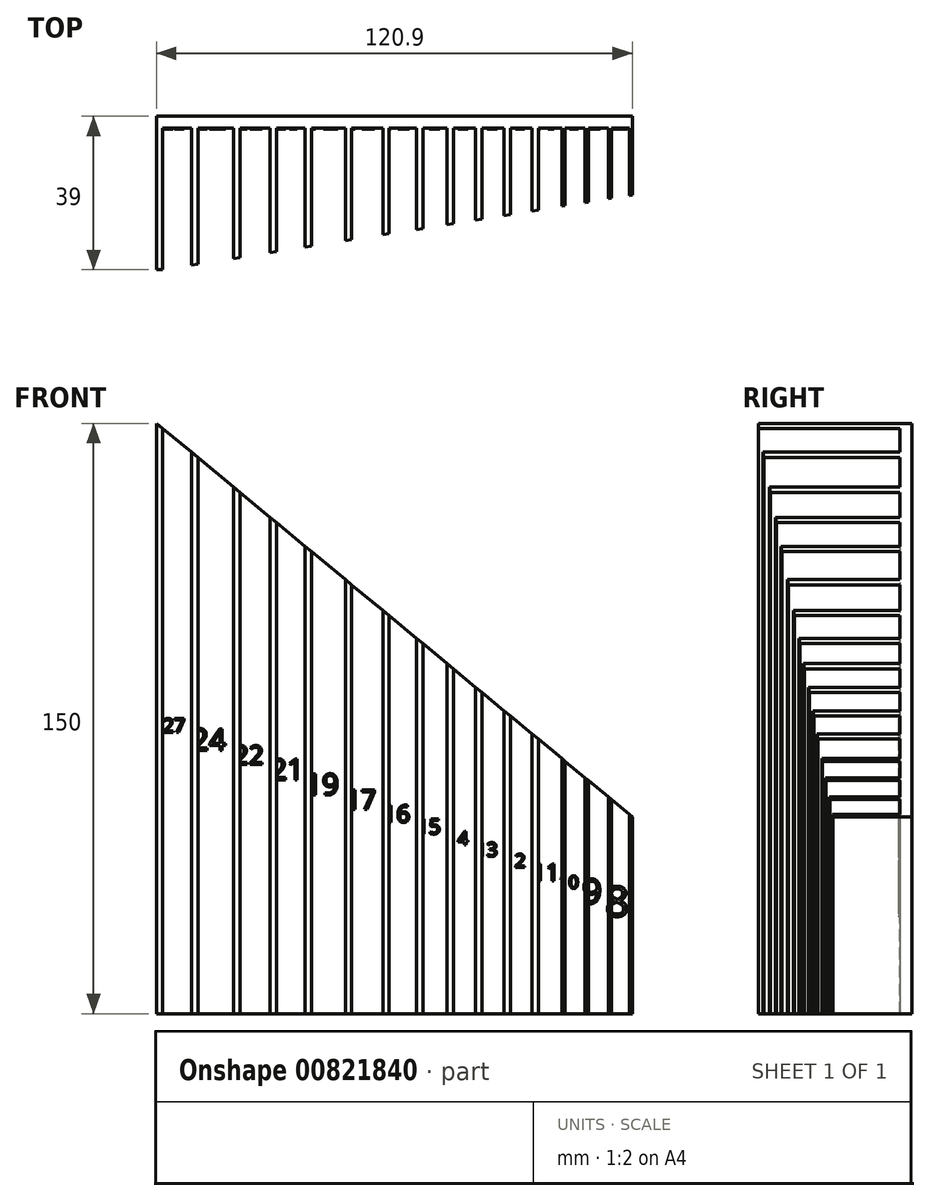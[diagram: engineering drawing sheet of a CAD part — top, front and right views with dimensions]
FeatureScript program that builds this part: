
annotation { "Feature Type Name" : "Feature", "Feature Type Description" : "" }
export const myFeature = defineFeature(function(context is Context, id is Id, definition is map)
    precondition{}
    {
        {
            var Q0;
            Q0=qCreatedBy(makeId("Front.planeOp"),FACE);
            var sketch = newSketch(context, id + "F0", { "sketchPlane" : qUnion([Q0])});
            skLineSegment(sketch, "E0", {"start": v(-64.3, 150) * mm, "end": v(-64.3, 0) * mm});
            skLineSegment(sketch, "E1", {"start": v(-64.3, 0) * mm, "end": v(56.6, 0) * mm});
            skLineSegment(sketch, "E2", {"start": v(56.6, 50) * mm, "end": v(-64.3, 150) * mm});
            skLineSegment(sketch, "E3", {"start": v(-64.3, 75) * mm, "end": v(56.6, 25) * mm, "construction": true});
            skLineSegment(sketch, "E4", {"start": v(56.6, 50) * mm, "end": v(56.6, 0) * mm});
            skSolve(sketch);
        }
        {
            var Q0;
            {var subQ0=sQuery(id+"F0.wireOp",EDGE,"E0");Q0=makeQuery(id+"F0.imprint","IMPRINT",FACE,{"disambiguationData":[TD([[makeQuery(id+"F0.imprint","IMPRINT",EDGE,{"derivedFrom":subQ0}),1.0]])]});}
            extrude(context, id + "F1", {"entities" : qUnion([Q0]), "depth" : 3 * mm, "offsetDistance" : 25 * mm});
        }
        {
            var Q0;
            Q0=makeQuery(id+"F1.opExtrude","CAP_FACE",FACE,{"disambiguationData":[OSD([sQuery(id+"F0.wireOp",EDGE,"E0"),sQuery(id+"F0.wireOp",EDGE,"E1"),sQuery(id+"F0.wireOp",EDGE,"0AxQtryP-TZW4-hSLZ-hSIb-DcVt68QFEk3i"),sQuery(id+"F0.wireOp",EDGE,"E2")])],"isStart":false});
            var sketch = newSketch(context, id + "F2", { "sketchPlane" : qUnion([Q0])});
            skLineSegment(sketch, "E5", {"start": v(-55.4, 142.64) * mm, "end": v(-55.4, 0) * mm});
            skLineSegment(sketch, "E6", {"start": v(-53.8, 141.32) * mm, "end": v(-53.8, 0) * mm});
            skLineSegment(sketch, "E7", {"start": v(-44.7, 133.79) * mm, "end": v(-44.7, 0) * mm});
            skLineSegment(sketch, "E8", {"start": v(-43.1, 132.46) * mm, "end": v(-43.1, 0) * mm});
            skLineSegment(sketch, "E9", {"start": v(-35.4, 126.1) * mm, "end": v(-35.4, 0) * mm});
            skLineSegment(sketch, "E10", {"start": v(-33.8, 124.77) * mm, "end": v(-33.8, 0) * mm});
            skLineSegment(sketch, "E11", {"start": v(-26.5, 118.73) * mm, "end": v(-26.5, 0) * mm});
            skLineSegment(sketch, "E12", {"start": v(-24.9, 117.41) * mm, "end": v(-24.9, 0) * mm});
            skLineSegment(sketch, "E13", {"start": v(-16.3, 110.3) * mm, "end": v(-16.3, 0) * mm});
            skLineSegment(sketch, "E14", {"start": v(-14.7, 108.97) * mm, "end": v(-14.7, 0) * mm});
            skLineSegment(sketch, "E15", {"start": v(-6.8, 102.44) * mm, "end": v(-6.8, 0) * mm});
            skLineSegment(sketch, "E16", {"start": v(-5.2, 101.12) * mm, "end": v(-5.2, 0) * mm});
            skLineSegment(sketch, "E17", {"start": v(1.8, 0) * mm, "end": v(1.8, 95.33) * mm});
            skLineSegment(sketch, "E18", {"start": v(3.4, 94) * mm, "end": v(3.4, 0) * mm});
            skLineSegment(sketch, "E19", {"start": v(9.5, 88.96) * mm, "end": v(9.5, 0) * mm});
            skLineSegment(sketch, "E20", {"start": v(11.1, 87.63) * mm, "end": v(11.1, 0) * mm});
            skLineSegment(sketch, "E21", {"start": v(16.8, 0) * mm, "end": v(16.8, 82.92) * mm});
            skLineSegment(sketch, "E22", {"start": v(18.4, 81.6) * mm, "end": v(18.4, 0) * mm});
            skLineSegment(sketch, "E23", {"start": v(24, 0) * mm, "end": v(24, 76.96) * mm});
            skLineSegment(sketch, "E24", {"start": v(25.6, 75.64) * mm, "end": v(25.6, 0) * mm});
            skLineSegment(sketch, "E25", {"start": v(31.1, 71.1) * mm, "end": v(31.1, 0) * mm});
            skLineSegment(sketch, "E26", {"start": v(32.7, 69.77) * mm, "end": v(32.7, 0) * mm});
            skLineSegment(sketch, "E27", {"start": v(38.7, 0) * mm, "end": v(38.7, 64.8) * mm});
            skLineSegment(sketch, "E28", {"start": v(39.5, 64.14) * mm, "end": v(39.5, 0) * mm});
            skLineSegment(sketch, "E29", {"start": v(44.6, 0) * mm, "end": v(44.6, 59.93) * mm});
            skLineSegment(sketch, "E30", {"start": v(45.4, 59.26) * mm, "end": v(45.4, 0) * mm});
            skLineSegment(sketch, "E31", {"start": v(50.5, 55.05) * mm, "end": v(50.5, 0) * mm});
            skLineSegment(sketch, "E32", {"start": v(51.3, 54.38) * mm, "end": v(51.3, 0) * mm});
            skLineSegment(sketch, "E33", {"start": v(-62.7, 148.68) * mm, "end": v(-62.7, 0) * mm});
            skLineSegment(sketch, "E34", {"start": v(55.8, 0) * mm, "end": v(55.8, 50.66) * mm});
            skSolve(sketch);
        }
        {
            var Q0;
            {var subQ0=sQuery(id+"F2.wireOp",EDGE,"E5");Q0=makeQuery(id+"F2.imprint","IMPRINT",FACE,{"disambiguationData":[TD([[makeQuery(id+"F2.imprint","IMPRINT",EDGE,{"derivedFrom":subQ0}),1.0]])]});}
            var Q1;
            {var subQ0=sQuery(id+"F2.wireOp",EDGE,"E7");Q1=makeQuery(id+"F2.imprint","IMPRINT",FACE,{"disambiguationData":[TD([[makeQuery(id+"F2.imprint","IMPRINT",EDGE,{"derivedFrom":subQ0}),1.0]])]});}
            var Q2;
            {var subQ0=sQuery(id+"F2.wireOp",EDGE,"E9");Q2=makeQuery(id+"F2.imprint","IMPRINT",FACE,{"disambiguationData":[TD([[makeQuery(id+"F2.imprint","IMPRINT",EDGE,{"derivedFrom":subQ0}),1.0]])]});}
            var Q3;
            {var subQ0=sQuery(id+"F2.wireOp",EDGE,"E11");Q3=makeQuery(id+"F2.imprint","IMPRINT",FACE,{"disambiguationData":[TD([[makeQuery(id+"F2.imprint","IMPRINT",EDGE,{"derivedFrom":subQ0}),1.0]])]});}
            var Q4;
            {var subQ0=sQuery(id+"F2.wireOp",EDGE,"E13");Q4=makeQuery(id+"F2.imprint","IMPRINT",FACE,{"disambiguationData":[TD([[makeQuery(id+"F2.imprint","IMPRINT",EDGE,{"derivedFrom":subQ0}),1.0]])]});}
            var Q5;
            {var subQ0=sQuery(id+"F2.wireOp",EDGE,"E15");Q5=makeQuery(id+"F2.imprint","IMPRINT",FACE,{"disambiguationData":[TD([[makeQuery(id+"F2.imprint","IMPRINT",EDGE,{"derivedFrom":subQ0}),1.0]])]});}
            var Q6;
            {var subQ0=sQuery(id+"F2.wireOp",EDGE,"E17");Q6=makeQuery(id+"F2.imprint","IMPRINT",FACE,{"disambiguationData":[TD([[makeQuery(id+"F2.imprint","IMPRINT",EDGE,{"derivedFrom":subQ0}),-1.0]])]});}
            var Q7;
            {var subQ0=sQuery(id+"F2.wireOp",EDGE,"E27");Q7=makeQuery(id+"F2.imprint","IMPRINT",FACE,{"disambiguationData":[TD([[makeQuery(id+"F2.imprint","IMPRINT",EDGE,{"derivedFrom":subQ0}),-1.0]])]});}
            var Q8;
            {var subQ0=sQuery(id+"F2.wireOp",EDGE,"E19");Q8=makeQuery(id+"F2.imprint","IMPRINT",FACE,{"disambiguationData":[TD([[makeQuery(id+"F2.imprint","IMPRINT",EDGE,{"derivedFrom":subQ0}),1.0]])]});}
            var Q9;
            {var subQ0=sQuery(id+"F2.wireOp",EDGE,"E21");Q9=makeQuery(id+"F2.imprint","IMPRINT",FACE,{"disambiguationData":[TD([[makeQuery(id+"F2.imprint","IMPRINT",EDGE,{"derivedFrom":subQ0}),-1.0]])]});}
            var Q10;
            {var subQ0=sQuery(id+"F2.wireOp",EDGE,"E23");Q10=makeQuery(id+"F2.imprint","IMPRINT",FACE,{"disambiguationData":[TD([[makeQuery(id+"F2.imprint","IMPRINT",EDGE,{"derivedFrom":subQ0}),-1.0]])]});}
            var Q11;
            {var subQ0=sQuery(id+"F2.wireOp",EDGE,"E25");Q11=makeQuery(id+"F2.imprint","IMPRINT",FACE,{"disambiguationData":[TD([[makeQuery(id+"F2.imprint","IMPRINT",EDGE,{"derivedFrom":subQ0}),1.0]])]});}
            var Q12;
            {var subQ0=sQuery(id+"F2.wireOp",EDGE,"E29");Q12=makeQuery(id+"F2.imprint","IMPRINT",FACE,{"disambiguationData":[TD([[makeQuery(id+"F2.imprint","IMPRINT",EDGE,{"derivedFrom":subQ0}),-1.0]])]});}
            var Q13;
            {var subQ0=sQuery(id+"F2.wireOp",EDGE,"E31");Q13=makeQuery(id+"F2.imprint","IMPRINT",FACE,{"disambiguationData":[TD([[makeQuery(id+"F2.imprint","IMPRINT",EDGE,{"derivedFrom":subQ0}),1.0]])]});}
            var Q14;
            {var subQ0=sQuery(id+"F2.wireOp",EDGE,"E34");Q14=makeQuery(id+"F2.imprint","IMPRINT",FACE,{"disambiguationData":[TD([[makeQuery(id+"F2.imprint","IMPRINT",EDGE,{"derivedFrom":subQ0}),-1.0]])]});}
            var Q15;
            {var subQ0=sQuery(id+"F2.wireOp",EDGE,"E33");Q15=makeQuery(id+"F2.imprint","IMPRINT",FACE,{"disambiguationData":[TD([[makeQuery(id+"F2.imprint","IMPRINT",EDGE,{"derivedFrom":subQ0}),-1.0]])]});}
            extrude(context, id + "F3", {"entities" : qUnion([Q0, Q1, Q2, Q3, Q4, Q5, Q6, Q7, Q8, Q9, Q10, Q11, Q12, Q13, Q14, Q15]), "operationType" : NewBodyOperationType.ADD, "depth" : 36 * mm, "offsetDistance" : 25 * mm});
        }
        {
            var Q0;
            Q0=qCreatedBy(makeId("Top.planeOp"),FACE);
            var sketch = newSketch(context, id + "F4", { "sketchPlane" : qUnion([Q0])});
            skLineSegment(sketch, "E35", {"start": v(-62.7, -39) * mm, "end": v(56.6, -20) * mm});
            skLineSegment(sketch, "E36", {"start": v(56.6, -39) * mm, "end": v(56.6, -20) * mm});
            skLineSegment(sketch, "E37", {"start": v(56.6, -39) * mm, "end": v(-62.7, -39) * mm});
            skSolve(sketch);
        }
        {
            var Q0;
            Q0 = qSketchRegion(id + "F4", true);
            extrude(context, id + "F5", {"entities" : qUnion([Q0]), "operationType" : NewBodyOperationType.REMOVE, "endBound" : BoundingType.THROUGH_ALL, "oppositeDirection" : true, "depth" : 25 * mm, "offsetDistance" : 25 * mm, "hasSecondDirection" : true, "secondDirectionBound" : SecondDirectionBoundingType.THROUGH_ALL, "secondDirectionOppositeDirection" : false, "secondDirectionDepth" : 25 * mm});
        }
        {
            var Q0;
            {var subQ0=sQuery(id+"F0.wireOp",EDGE,"E4");var subQ2=sQuery(id+"F0.wireOp",EDGE,"E2");var subQ5=sQuery(id+"F0.wireOp",EDGE,"E0");var subQ9=sQuery(id+"F0.wireOp",EDGE,"E1");var subQ34=sQuery(id+"F2.wireOp",EDGE,"E5");Q0=makeQuery(id+"F3.boolean.opBoolean","SPLIT",FACE,{"disambiguationData":[TD([makeQuery(id+"F3.opExtrude","SWEPT_FACE",FACE,{"disambiguationData":[OSD([subQ34])]})])],"derivedFrom":makeQuery(id+"F1.opExtrude","CAP_FACE",FACE,{"disambiguationData":[OSD([subQ5,subQ9,subQ2,subQ0])],"isStart":false})});}
            var sketch = newSketch(context, id + "F6", { "sketchPlane" : qUnion([Q0])});
            skLineSegment(sketch, "E38", {"start": v(-64.3, 75) * mm, "end": v(50.5, 27.52) * mm, "construction": true});
            skText(sketch, "E39", { "text": "27", "fontName": "OpenSans-Regular.ttf"});
            skText(sketch, "E40", { "text": "24\n", "fontName": "OpenSans-Regular.ttf"});
            skPoint(sketch, "E41", {"position": v(-49.25, 68.78) * mm});
            skPoint(sketch, "E42", {"position": v(-59.05, 72.83) * mm});
            skPoint(sketch, "E43", {"position": v(-39.25, 64.64) * mm});
            skPoint(sketch, "E44", {"position": v(-30.15, 60.88) * mm});
            skPoint(sketch, "E45", {"position": v(-20.6, 56.93) * mm});
            skPoint(sketch, "E46", {"position": v(-10.75, 52.85) * mm});
            skPoint(sketch, "E47", {"position": v(-1.7, 49.11) * mm});
            skPoint(sketch, "E48", {"position": v(6.45, 45.74) * mm});
            skText(sketch, "E49", { "text": "22", "fontName": "OpenSans-Regular.ttf"});
            skText(sketch, "E50", { "text": "21\n", "fontName": "OpenSans-Regular.ttf"});
            skText(sketch, "E51", { "text": "19", "fontName": "OpenSans-Regular.ttf"});
            skText(sketch, "E52", { "text": "17", "fontName": "OpenSans-Regular.ttf"});
            skText(sketch, "E53", { "text": "16", "fontName": "OpenSans-Regular.ttf"});
            skText(sketch, "E54", { "text": "15", "fontName": "OpenSans-Regular.ttf"});
            skText(sketch, "E55", { "text": "14\n", "fontName": "OpenSans-Regular.ttf"});
            skText(sketch, "E56", { "text": "13", "fontName": "OpenSans-Regular.ttf"});
            skText(sketch, "E57", { "text": "12", "fontName": "OpenSans-Regular.ttf"});
            skText(sketch, "E58", { "text": "11", "fontName": "OpenSans-Regular.ttf"});
            skText(sketch, "E59", { "text": "10", "fontName": "OpenSans-Regular.ttf"});
            skText(sketch, "E60", { "text": "9", "fontName": "OpenSans-Regular.ttf"});
            skText(sketch, "E61", { "text": "8", "fontName": "OpenSans-Regular.ttf"});
            skPoint(sketch, "E62", {"position": v(13.95, 42.64) * mm});
            skPoint(sketch, "E63", {"position": v(21.2, 39.64) * mm});
            skPoint(sketch, "E64", {"position": v(28.35, 36.68) * mm});
            skPoint(sketch, "E65", {"position": v(35.7, 33.64) * mm});
            skPoint(sketch, "E66", {"position": v(42.05, 31.02) * mm});
            skPoint(sketch, "E67", {"position": v(47.95, 28.58) * mm});
            skPoint(sketch, "E68", {"position": v(53.55, 26.26) * mm});
            const initialGuessF6  = {"E39": [-0.0627, 0.07146, 1, 0, 0.00355], "E40": [-0.0554, 0.0669, 1, 0, 0.00551], "E49": [-0.0447, 0.0633, 1, 0, 0.0048], "E50": [-0.0354, 0.05942, 1, 0, 0.00533], "E51": [-0.0265, 0.05561, 1, 0, 0.00536], "E52": [-0.0163, 0.05193, 1, 0, 0.00491], "E53": [-0.0068, 0.04862, 1, 0, 0.00435], "E54": [0.0018, 0.04565, 1, 0, 0.00382], "E55": [0.0095, 0.04286, 1, 0, 0.00345], "E56": [0.0168, 0.03995, 1, 0, 0.0035], "E57": [0.024, 0.03715, 1, 0, 0.00343], "E58": [0.0311, 0.03376, 1, 0, 0.00438], "E59": [0.0379, 0.03185, 1, 0, 0.00317], "E60": [0.0438, 0.02794, 1, 0, 0.0063], "E61": [0.0497, 0.02472, 1, 0, 0.00763]};
            skSetInitialGuess(sketch, initialGuessF6);
            skSolve(sketch);
        }
        {
            var Q0;
            Q0 = qSketchRegion(id + "F6", true);
            extrude(context, id + "F7", {"entities" : qUnion([Q0]), "operationType" : NewBodyOperationType.ADD, "depth" : 0.3 * mm, "offsetDistance" : 25 * mm});
        }
    });
